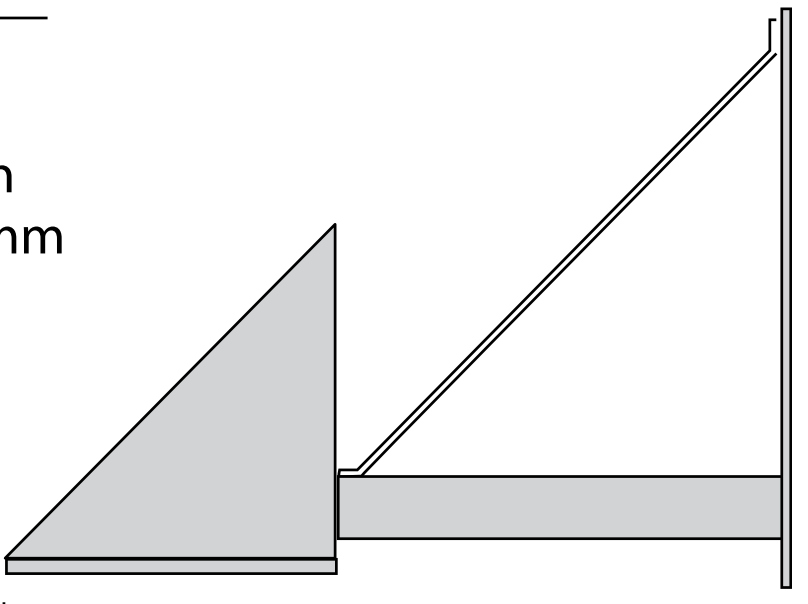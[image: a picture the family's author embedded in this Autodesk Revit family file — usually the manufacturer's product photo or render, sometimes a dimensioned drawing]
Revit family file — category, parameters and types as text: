
# Revit family: M2PXA
name_source: partatom
category: Lighting Fixtures
units: mm (PartAtom-declared; Revit-internal decimal feet)

## family parameters
Cut with Voids When Loaded = No
Host = Face
Light Source = No
OmniClass Number = 23.80.70.14.14
OmniClass Title = Exterior Floodlights
Part Type = Normal
Room Calculation Point = No
Round Connector Dimension = Use Diameter
Shared = Yes

## types (1)
- M2PXA
    Apparent Load = 0 VA
    Default Elevation = 48 "
    Description = Horizontal reflector downlight with extended arm
    Finish = Die Cast Aluminium
    Finish 2 = Silicon Gasket
    Glass = Glass-Finish
    Lamp = One
    Manufacturer = Architectural Area Lighting
    Model = M2PXA
    Photometric = M2PXA_01 : M2PXA-T5-32LED-5K-700
    Pole Height = 100 "
    URL = https://www.currentlighting.com
    Wattage Comments = 57 and 70 watts High Output Fluorescent

## geometry (parser evidence)
native form markers: Blend x2, Sweep x6
no freeform markers — native parametric forms only
